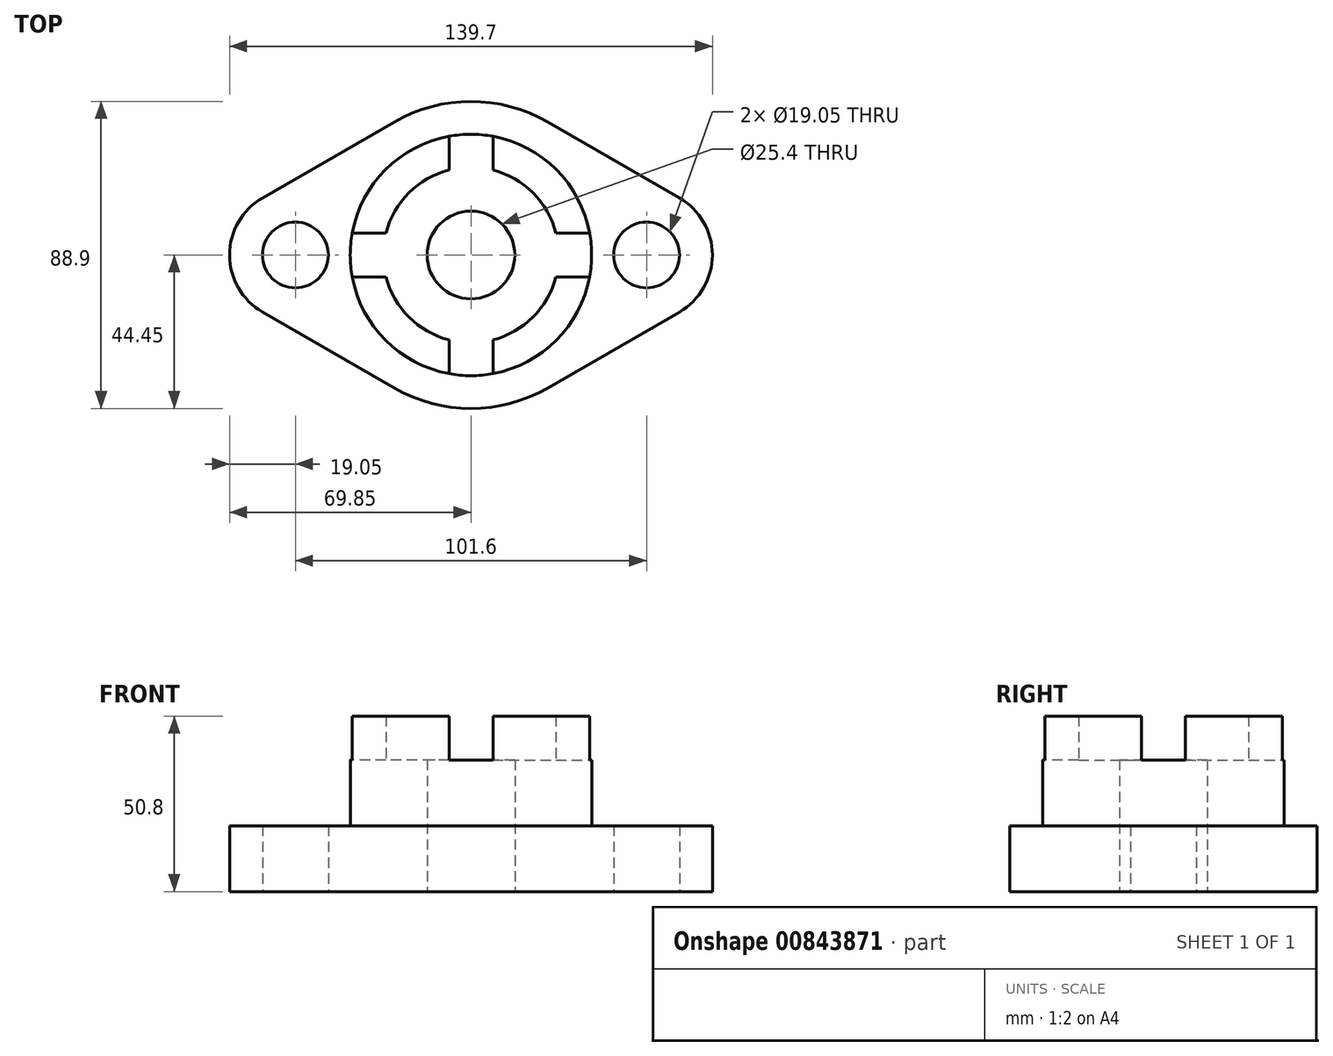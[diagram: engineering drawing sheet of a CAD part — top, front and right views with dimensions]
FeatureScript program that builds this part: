
annotation { "Feature Type Name" : "Feature", "Feature Type Description" : "" }
export const myFeature = defineFeature(function(context is Context, id is Id, definition is map)
    precondition{}
    {
        {
            var Q0;
            Q0=qCreatedBy(makeId("Top.planeOp"),FACE);
            var sketch = newSketch(context, id + "F0", { "sketchPlane" : qUnion([Q0])});
            skCircle(sketch, "E0", {"center": v(0, 0) * mm, "radius": 12.7 * mm});
            skCircle(sketch, "E1", {"center": v(0, 0) * mm, "radius": 25.4 * mm});
            skCircle(sketch, "E2", {"center": v(0, 0) * mm, "radius": 34.93 * mm});
            skLineSegment(sketch, "E3", {"start": v(0, 0) * mm, "end": v(50.8, 0) * mm});
            skLineSegment(sketch, "E4", {"start": v(0, 0) * mm, "end": v(-34.93, 0) * mm});
            skCircle(sketch, "E5", {"center": v(-50.8, 0) * mm, "radius": 9.53 * mm});
            skCircle(sketch, "E6", {"center": v(50.8, 0) * mm, "radius": 9.53 * mm});
            skLineSegment(sketch, "E7", {"start": v(0, 0) * mm, "end": v(0, -34.93) * mm});
            skLineSegment(sketch, "E8", {"start": v(0, 0) * mm, "end": v(34.93, 0) * mm});
            skLineSegment(sketch, "E9", {"start": v(0, 0) * mm, "end": v(0, 34.93) * mm});
            skLineSegment(sketch, "E10", {"start": v(-34.34, -6.35) * mm, "end": v(-24.6, -6.35) * mm});
            skLineSegment(sketch, "E11", {"start": v(-34.34, 6.35) * mm, "end": v(-24.6, 6.35) * mm});
            skLineSegment(sketch, "E12", {"start": v(-6.35, -34.34) * mm, "end": v(-6.35, -24.6) * mm});
            skLineSegment(sketch, "E13", {"start": v(6.35, -34.34) * mm, "end": v(6.35, -24.6) * mm});
            skLineSegment(sketch, "E14", {"start": v(34.34, 6.35) * mm, "end": v(24.6, 6.35) * mm});
            skLineSegment(sketch, "E15", {"start": v(34.34, -6.35) * mm, "end": v(24.6, -6.35) * mm});
            skLineSegment(sketch, "E16", {"start": v(-6.35, 34.93) * mm, "end": v(-6.35, 24.6) * mm});
            skLineSegment(sketch, "E17", {"start": v(6.35, 34.93) * mm, "end": v(6.35, 24.6) * mm});
            skLineSegment(sketch, "E18", {"start": v(0, 0) * mm, "end": v(0, 44.45) * mm});
            skLineSegment(sketch, "E19", {"start": v(-50.8, 0) * mm, "end": v(-69.85, 0) * mm});
            skLineSegment(sketch, "E20", {"start": v(50.8, 0) * mm, "end": v(69.85, 0) * mm});
            skLineSegment(sketch, "E21", {"start": v(-50.8, 0) * mm, "end": v(-60.33, 0) * mm});
            skLineSegment(sketch, "E22", {"start": v(-60.33, 0) * mm, "end": v(-69.85, 0) * mm});
            skArc(sketch, "E23", {"start": v(60.33, -16.5) * mm, "mid": v(69.85, 0) * mm, "end": v(60.33, 16.5) * mm});
            skArc(sketch, "E24", {"start": v(-22.23, -38.5) * mm, "mid": v(0, -44.45) * mm, "end": v(22.22, -38.5) * mm});
            skLineSegment(sketch, "E25", {"start": v(-60.33, 16.5) * mm, "end": v(-22.23, 38.5) * mm});
            skLineSegment(sketch, "E26", {"start": v(-60.33, -16.5) * mm, "end": v(-22.23, -38.5) * mm});
            skLineSegment(sketch, "E27", {"start": v(60.33, -16.5) * mm, "end": v(22.22, -38.5) * mm});
            skLineSegment(sketch, "E28", {"start": v(60.33, 16.5) * mm, "end": v(22.23, 38.5) * mm});
            skArc(sketch, "E29.trimOffspring", {"start": v(-60.33, 16.5) * mm, "mid": v(-69.85, 0) * mm, "end": v(-60.33, -16.5) * mm});
            skLineSegment(sketch, "E30.trimOffspring", {"start": v(-41.28, 0) * mm, "end": v(-50.8, 0) * mm});
            skPoint(sketch, "E31.orphan", {"position": v(0, -44.45) * mm});
            skArc(sketch, "E32.trimOffspring", {"start": v(22.22, 38.5) * mm, "mid": v(0, 44.45) * mm, "end": v(-22.22, 38.5) * mm});
            skPoint(sketch, "E33.start.orphan", {"position": v(60.33, 0) * mm});
            skSolve(sketch);
        }
        {
            var Q0;
            Q0 = qSketchRegion(id + "F0", true);
            extrude(context, id + "F1", {"entities" : qUnion([Q0]), "depth" : 19.05 * mm, "offsetDistance" : 25.4 * mm});
        }
        {
            var Q0;
            {var subQ0=sQuery(id+"F0.wireOp",EDGE,"E10");Q0=makeQuery(id+"F0.imprint","IMPRINT",FACE,{"disambiguationData":[TD([[makeQuery(id+"F0.imprint","IMPRINT",EDGE,{"derivedFrom":subQ0}),-1.0]])]});}
            var Q1;
            {var subQ0=sQuery(id+"F0.wireOp",EDGE,"E10");Q1=makeQuery(id+"F0.imprint","IMPRINT",FACE,{"disambiguationData":[TD([[makeQuery(id+"F0.imprint","IMPRINT",EDGE,{"derivedFrom":subQ0}),1.0]])]});}
            var Q2;
            {var subQ0=sQuery(id+"F0.wireOp",EDGE,"E11");Q2=makeQuery(id+"F0.imprint","IMPRINT",FACE,{"disambiguationData":[TD([[makeQuery(id+"F0.imprint","IMPRINT",EDGE,{"derivedFrom":subQ0}),-1.0]])]});}
            var Q3;
            {var subQ0=sQuery(id+"F0.wireOp",EDGE,"E11");Q3=makeQuery(id+"F0.imprint","IMPRINT",FACE,{"disambiguationData":[TD([[makeQuery(id+"F0.imprint","IMPRINT",EDGE,{"derivedFrom":subQ0}),1.0]])]});}
            var Q4;
            {var subQ0=sQuery(id+"F0.wireOp",EDGE,"E16");var subQ1=sQuery(id+"F0.wireOp",EDGE,"E1");var subQ2=makeQuery(id+"F0.imprint","INTERSECT",VERTEX,{"derivedFrom":[subQ1,subQ0]});Q4=makeQuery(id+"F0.imprint","IMPRINT",FACE,{"disambiguationData":[TD([[makeQuery(id+"F0.imprint","IMPRINT",EDGE,{"disambiguationData":[TD([[subQ2,1.0]])],"derivedFrom":subQ1}),-1.0]])]});}
            var Q5;
            {var subQ0=sQuery(id+"F0.wireOp",EDGE,"E17");var subQ1=sQuery(id+"F0.wireOp",EDGE,"E1");var subQ2=makeQuery(id+"F0.imprint","INTERSECT",VERTEX,{"derivedFrom":[subQ1,subQ0]});Q5=makeQuery(id+"F0.imprint","IMPRINT",FACE,{"disambiguationData":[TD([[makeQuery(id+"F0.imprint","IMPRINT",EDGE,{"disambiguationData":[TD([[subQ2,-1.0]])],"derivedFrom":subQ1}),-1.0]])]});}
            var Q6;
            {var subQ0=sQuery(id+"F0.wireOp",EDGE,"E14");Q6=makeQuery(id+"F0.imprint","IMPRINT",FACE,{"disambiguationData":[TD([[makeQuery(id+"F0.imprint","IMPRINT",EDGE,{"derivedFrom":subQ0}),-1.0]])]});}
            var Q7;
            {var subQ0=sQuery(id+"F0.wireOp",EDGE,"E14");Q7=makeQuery(id+"F0.imprint","IMPRINT",FACE,{"disambiguationData":[TD([[makeQuery(id+"F0.imprint","IMPRINT",EDGE,{"derivedFrom":subQ0}),1.0]])]});}
            var Q8;
            {var subQ0=sQuery(id+"F0.wireOp",EDGE,"E13");Q8=makeQuery(id+"F0.imprint","IMPRINT",FACE,{"disambiguationData":[TD([[makeQuery(id+"F0.imprint","IMPRINT",EDGE,{"derivedFrom":subQ0}),1.0]])]});}
            var Q9;
            {var subQ0=sQuery(id+"F0.wireOp",EDGE,"E12");Q9=makeQuery(id+"F0.imprint","IMPRINT",FACE,{"disambiguationData":[TD([[makeQuery(id+"F0.imprint","IMPRINT",EDGE,{"derivedFrom":subQ0}),-1.0]])]});}
            var Q10;
            {var subQ0=sQuery(id+"F0.wireOp",EDGE,"E15");Q10=makeQuery(id+"F0.imprint","IMPRINT",FACE,{"disambiguationData":[TD([[makeQuery(id+"F0.imprint","IMPRINT",EDGE,{"derivedFrom":subQ0}),-1.0]])]});}
            var Q11;
            {var subQ0=sQuery(id+"F0.wireOp",EDGE,"E13");Q11=makeQuery(id+"F0.imprint","IMPRINT",FACE,{"disambiguationData":[TD([[makeQuery(id+"F0.imprint","IMPRINT",EDGE,{"derivedFrom":subQ0}),-1.0]])]});}
            var Q12;
            {var subQ3=sQuery(id+"F0.wireOp",EDGE,"E4");var subQ7=sQuery(id+"F0.wireOp",EDGE,"E0");var subQ8=makeQuery(id+"F0.imprint","INTERSECT",VERTEX,{"derivedFrom":[subQ7,subQ3]});Q12=makeQuery(id+"F0.imprint","IMPRINT",FACE,{"disambiguationData":[TD([[makeQuery(id+"F0.imprint","IMPRINT",EDGE,{"disambiguationData":[TD([[subQ8,-1.0]])],"derivedFrom":subQ7}),-1.0]])]});}
            var Q13;
            {var subQ2=sQuery(id+"F0.wireOp",EDGE,"E8");var subQ5=sQuery(id+"F0.wireOp",EDGE,"E0");var subQ6=makeQuery(id+"F0.imprint","INTERSECT",VERTEX,{"derivedFrom":[subQ5,subQ2]});Q13=makeQuery(id+"F0.imprint","IMPRINT",FACE,{"disambiguationData":[TD([[makeQuery(id+"F0.imprint","IMPRINT",EDGE,{"disambiguationData":[TD([[subQ6,1.0]])],"derivedFrom":subQ5}),-1.0]])]});}
            var Q14;
            {var subQ2=sQuery(id+"F0.wireOp",EDGE,"E18");var subQ7=sQuery(id+"F0.wireOp",EDGE,"E0");var subQ8=makeQuery(id+"F0.imprint","INTERSECT",VERTEX,{"derivedFrom":[subQ7,subQ2]});Q14=makeQuery(id+"F0.imprint","IMPRINT",FACE,{"disambiguationData":[TD([[makeQuery(id+"F0.imprint","IMPRINT",EDGE,{"disambiguationData":[TD([[subQ8,1.0]])],"derivedFrom":subQ7}),-1.0]])]});}
            var Q15;
            {var subQ5=sQuery(id+"F0.wireOp",EDGE,"E18");var subQ6=sQuery(id+"F0.wireOp",EDGE,"E0");var subQ7=makeQuery(id+"F0.imprint","INTERSECT",VERTEX,{"derivedFrom":[subQ6,subQ5]});Q15=makeQuery(id+"F0.imprint","IMPRINT",FACE,{"disambiguationData":[TD([[makeQuery(id+"F0.imprint","IMPRINT",EDGE,{"disambiguationData":[TD([[subQ7,-1.0]])],"derivedFrom":subQ6}),-1.0]])]});}
            extrude(context, id + "F2", {"entities" : qUnion([Q0, Q1, Q2, Q3, Q4, Q5, Q6, Q7, Q8, Q9, Q10, Q11, Q12, Q13, Q14, Q15]), "operationType" : NewBodyOperationType.ADD, "depth" : 38.1 * mm, "offsetDistance" : 25.4 * mm});
        }
        {
            var Q0;
            {var subQ0=sQuery(id+"F0.wireOp",EDGE,"E10");Q0=makeQuery(id+"F0.imprint","IMPRINT",FACE,{"disambiguationData":[TD([[makeQuery(id+"F0.imprint","IMPRINT",EDGE,{"derivedFrom":subQ0}),-1.0]])]});}
            var Q1;
            {var subQ0=sQuery(id+"F0.wireOp",EDGE,"E13");Q1=makeQuery(id+"F0.imprint","IMPRINT",FACE,{"disambiguationData":[TD([[makeQuery(id+"F0.imprint","IMPRINT",EDGE,{"derivedFrom":subQ0}),-1.0]])]});}
            var Q2;
            {var subQ0=sQuery(id+"F0.wireOp",EDGE,"E14");Q2=makeQuery(id+"F0.imprint","IMPRINT",FACE,{"disambiguationData":[TD([[makeQuery(id+"F0.imprint","IMPRINT",EDGE,{"derivedFrom":subQ0}),-1.0]])]});}
            var Q3;
            {var subQ0=sQuery(id+"F0.wireOp",EDGE,"E11");Q3=makeQuery(id+"F0.imprint","IMPRINT",FACE,{"disambiguationData":[TD([[makeQuery(id+"F0.imprint","IMPRINT",EDGE,{"derivedFrom":subQ0}),1.0]])]});}
            extrude(context, id + "F3", {"entities" : qUnion([Q0, Q1, Q2, Q3]), "operationType" : NewBodyOperationType.ADD, "depth" : 50.8 * mm, "offsetDistance" : 25.4 * mm});
        }
    });
